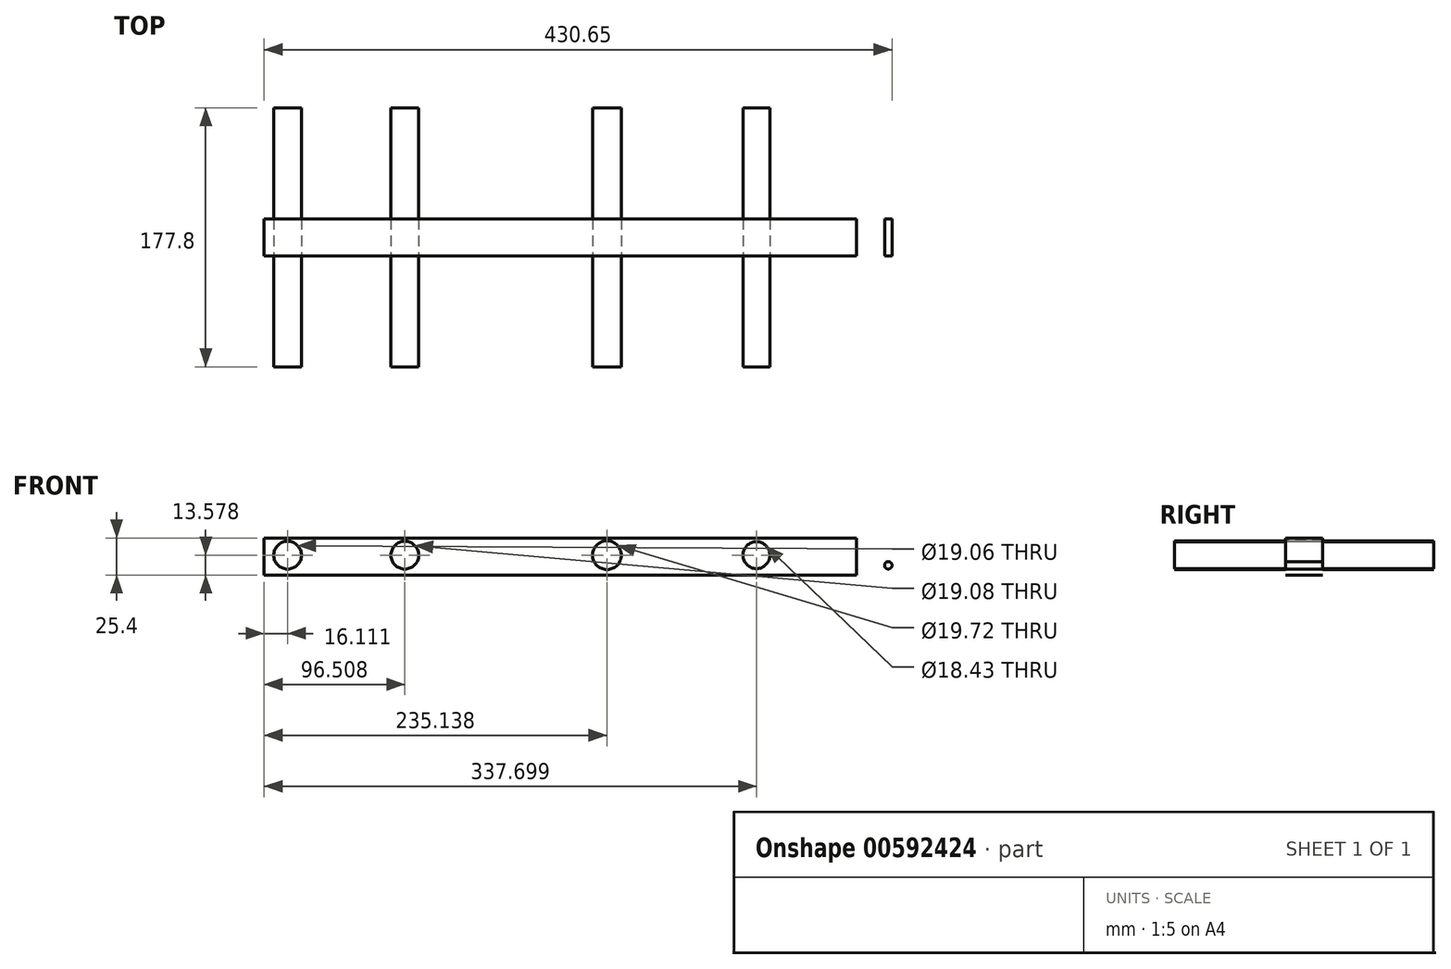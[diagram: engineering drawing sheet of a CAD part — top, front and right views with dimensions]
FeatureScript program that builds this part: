
annotation { "Feature Type Name" : "Feature", "Feature Type Description" : "" }
export const myFeature = defineFeature(function(context is Context, id is Id, definition is map)
    precondition{}
    {
        {
            var Q0;
            Q0=qCreatedBy(makeId("Front.planeOp"),FACE);
            var sketch = newSketch(context, id + "F0", { "sketchPlane" : qUnion([Q0])});
            skLineSegment(sketch, "E0.bottom", {"start": v(-211.8, 18.76) * mm, "end": v(194.6, 18.76) * mm});
            skLineSegment(sketch, "E0.top", {"start": v(-211.8, -6.64) * mm, "end": v(194.6, -6.64) * mm});
            skLineSegment(sketch, "E0.left", {"start": v(-211.8, 18.76) * mm, "end": v(-211.8, -6.64) * mm});
            skLineSegment(sketch, "E0.right", {"start": v(194.6, 18.76) * mm, "end": v(194.6, -6.64) * mm});
            skCircle(sketch, "E1", {"center": v(-195.69, 6.94) * mm, "radius": 9.53 * mm});
            skCircle(sketch, "E2", {"center": v(216.3, 0) * mm, "radius": 2.55 * mm});
            skCircle(sketch, "E3", {"center": v(-115.3, 6.94) * mm, "radius": 9.54 * mm});
            skCircle(sketch, "E4", {"center": v(23.34, 6.94) * mm, "radius": 9.86 * mm});
            skCircle(sketch, "E5", {"center": v(125.9, 6.94) * mm, "radius": 9.22 * mm});
            skSolve(sketch);
        }
        {
            var Q0;
            Q0 = qSketchRegion(id + "F0", true);
            extrude(context, id + "F1", {"entities" : qUnion([Q0]), "depth" : 25.4 * mm, "offsetDistance" : 25.4 * mm});
        }
        {
            var Q0;
            Q0=makeQuery(id+"F1.opExtrude","CAP_FACE",FACE,{"disambiguationData":[OSD([sQuery(id+"F0.wireOp",EDGE,"E0.bottom"),sQuery(id+"F0.wireOp",EDGE,"E0.top"),sQuery(id+"F0.wireOp",EDGE,"E0.left"),sQuery(id+"F0.wireOp",EDGE,"E0.right"),sQuery(id+"F0.wireOp",EDGE,"E1"),sQuery(id+"F0.wireOp",EDGE,"E3"),sQuery(id+"F0.wireOp",EDGE,"E4"),sQuery(id+"F0.wireOp",EDGE,"E5")])],"isStart":true});
            var sketch = newSketch(context, id + "F2", { "sketchPlane" : qUnion([Q0])});
            skCircle(sketch, "E6.0", {"center": v(-125.9, 6.94) * mm, "radius": 9.22 * mm});
            skCircle(sketch, "E7.0", {"center": v(-23.34, 6.94) * mm, "radius": 9.86 * mm});
            skCircle(sketch, "E8.0", {"center": v(115.3, 6.94) * mm, "radius": 9.54 * mm});
            skCircle(sketch, "E9.0", {"center": v(195.69, 6.94) * mm, "radius": 9.53 * mm});
            skSolve(sketch);
        }
        {
            var Q0;
            Q0 = qSketchRegion(id + "F2", true);
            extrude(context, id + "F3", {"entities" : qUnion([Q0]), "depth" : 76.2 * mm, "offsetDistance" : 25.4 * mm, "hasSecondDirection" : true, "secondDirectionOppositeDirection" : true, "secondDirectionDepth" : 101.6 * mm});
        }
    });
